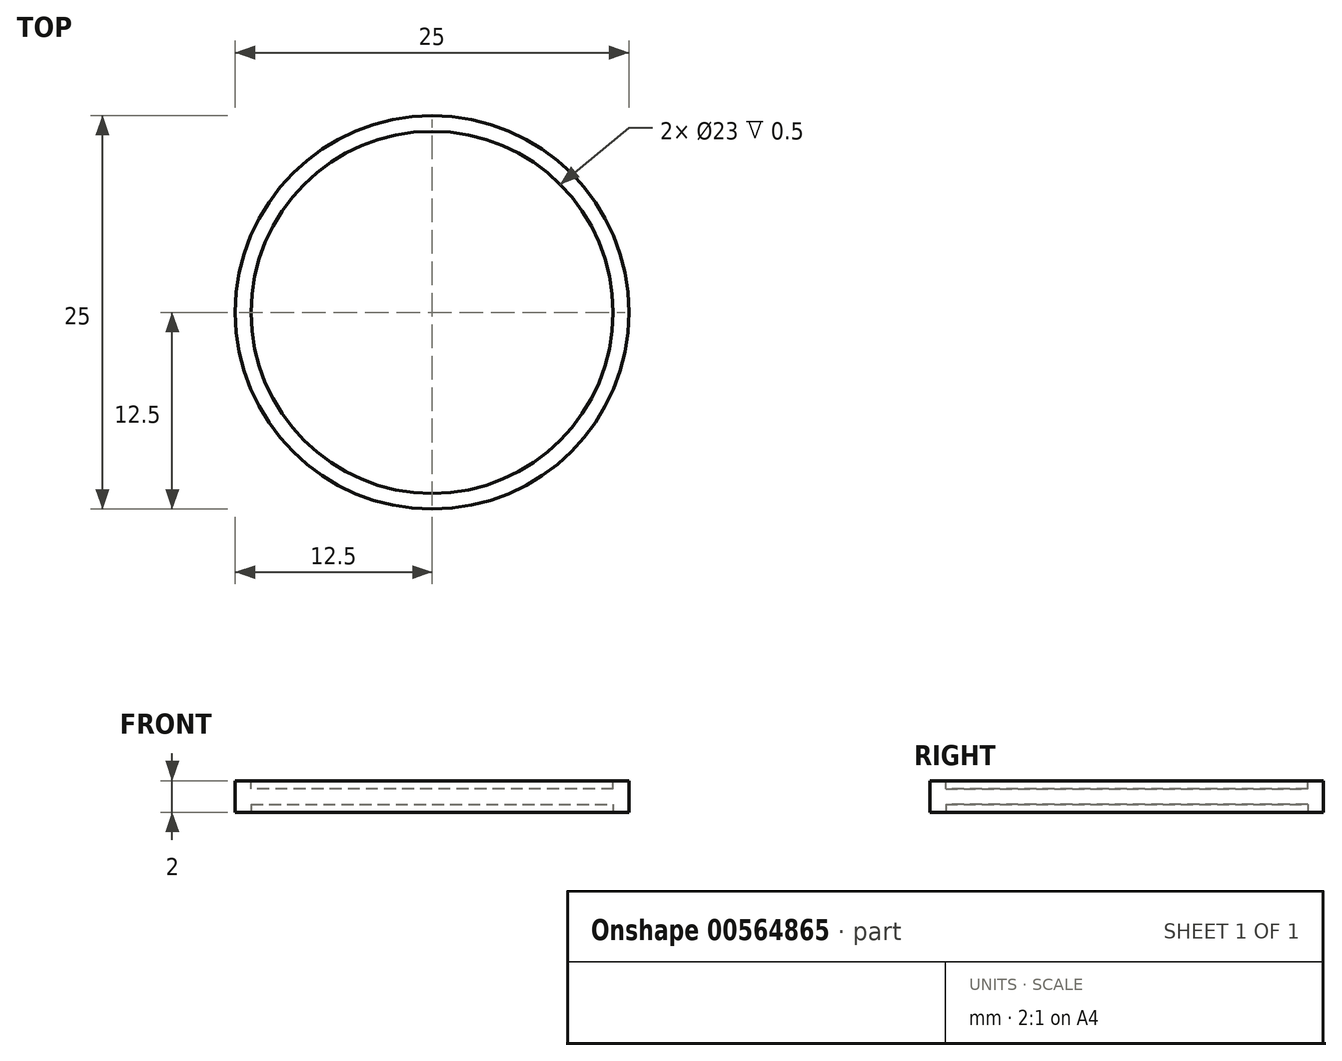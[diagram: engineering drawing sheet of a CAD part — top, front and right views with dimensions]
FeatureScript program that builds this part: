
annotation { "Feature Type Name" : "Feature", "Feature Type Description" : "" }
export const myFeature = defineFeature(function(context is Context, id is Id, definition is map)
    precondition{}
    {
        {
            assignVariable(context, id + "F0", {"name" : "ImpressionDepth", "anyValue" : 0.5});
        }
        {
            var Q0;
            Q0=qCreatedBy(makeId("Top.planeOp"),FACE);
            var sketch = newSketch(context, id + "F1", { "sketchPlane" : qUnion([Q0])});
            skCircle(sketch, "E0", {"center": v(0, 0) * mm, "radius": 12.5 * mm});
            skSolve(sketch);
        }
        {
            var Q0;
            Q0=qSketchRegion(id+"F1",true);
            extrude(context, id + "F2", {"entities" : qUnion([Q0]), "depth" : 2 * mm});
        }
        {
            var Q0;
            Q0=makeQuery(id+"F2.opExtrude","CAP_FACE",FACE,{"disambiguationData":[OSD([sQuery(id+"F1.wireOp",EDGE,"E0")])],"isStart":false});
            var sketch = newSketch(context, id + "F3", { "sketchPlane" : qUnion([Q0])});
            skCircle(sketch, "E1.0", {"center": v(0, 0) * mm, "radius": 11.5 * mm});
            skSolve(sketch);
        }
        {
            var Q0;
            Q0=qSketchRegion(id+"F3",true);
            extrude(context, id + "F4", {"entities" : qUnion([Q0]), "operationType" : NewBodyOperationType.REMOVE, "oppositeDirection" : true, "depth" : (getVariable(context, 'ImpressionDepth')) * mm});
        }
        {
            var Q0;
            Q0=makeQuery(id+"F2.opExtrude","CAP_FACE",FACE,{"disambiguationData":[OSD([sQuery(id+"F1.wireOp",EDGE,"E0")])],"isStart":true});
            var sketch = newSketch(context, id + "F5", { "sketchPlane" : qUnion([Q0])});
            skCircle(sketch, "E2.0", {"center": v(0, 0) * mm, "radius": 11.5 * mm});
            skSolve(sketch);
        }
        {
            var Q0;
            Q0=qSketchRegion(id+"F5",true);
            extrude(context, id + "F6", {"entities" : qUnion([Q0]), "operationType" : NewBodyOperationType.REMOVE, "oppositeDirection" : true, "depth" : (getVariable(context, 'ImpressionDepth')) * mm});
        }
    });
